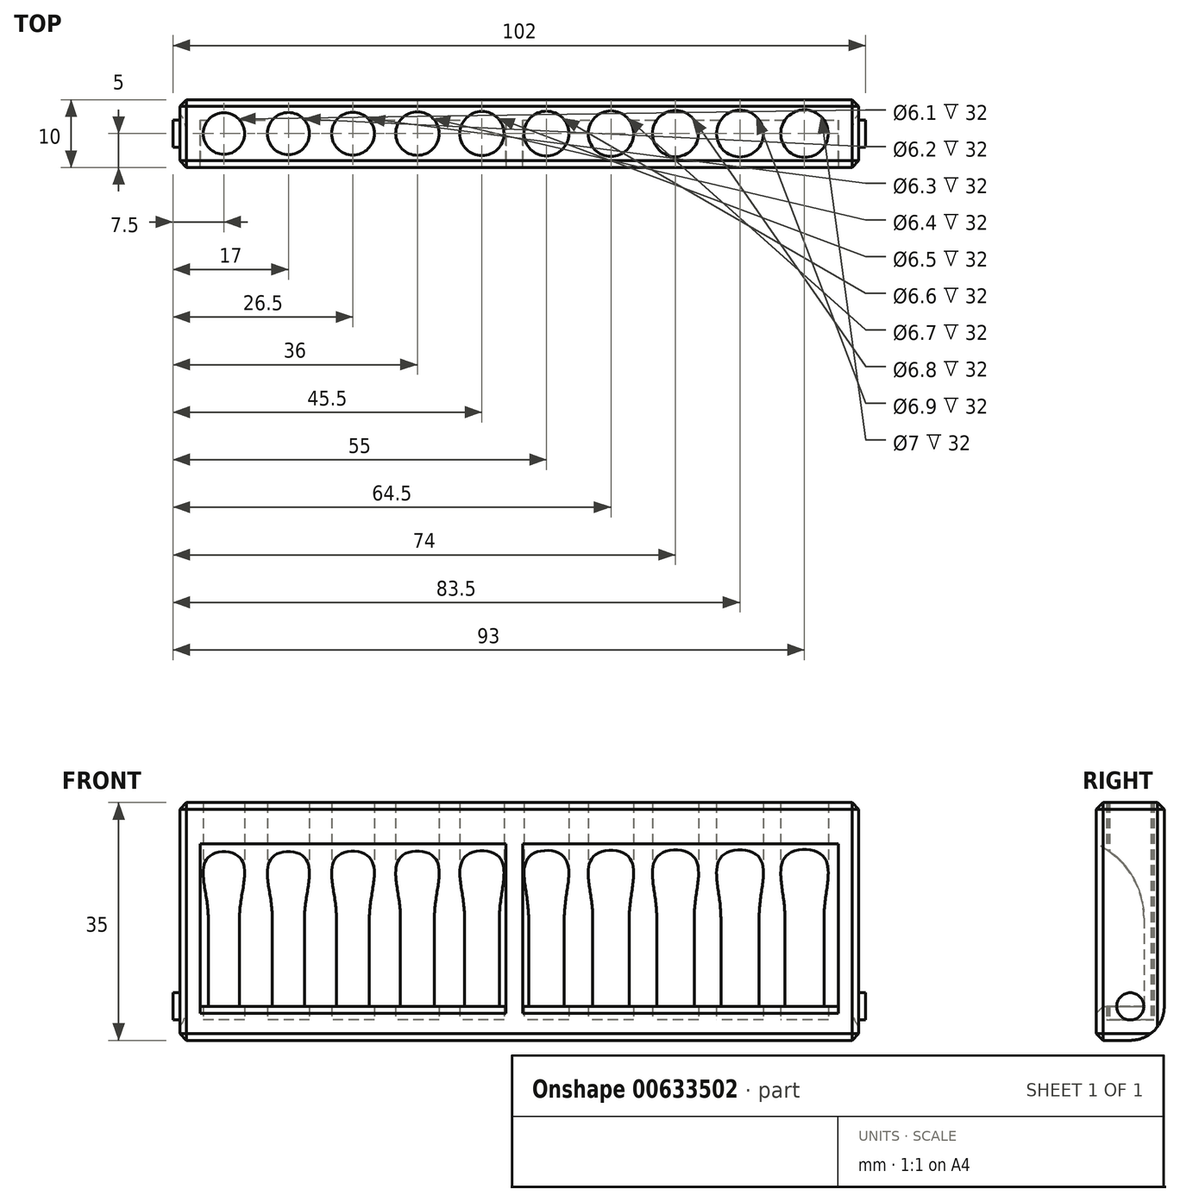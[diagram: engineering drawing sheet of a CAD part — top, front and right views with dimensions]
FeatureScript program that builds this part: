
annotation { "Feature Type Name" : "Feature", "Feature Type Description" : "" }
export const myFeature = defineFeature(function(context is Context, id is Id, definition is map)
    precondition{}
    {
        {
            var Q0;
            Q0=qCreatedBy(makeId("Top.planeOp"),FACE);
            var sketch = newSketch(context, id + "F0", { "sketchPlane" : qUnion([Q0])});
            skLineSegment(sketch, "E0.bottom", {"start": v(0, 0) * mm, "end": v(-100, 0) * mm});
            skLineSegment(sketch, "E0.top", {"start": v(0, -10) * mm, "end": v(-100, -10) * mm});
            skLineSegment(sketch, "E0.left", {"start": v(0, 0) * mm, "end": v(0, -10) * mm});
            skLineSegment(sketch, "E0.right", {"start": v(-100, 0) * mm, "end": v(-100, -10) * mm});
            skSolve(sketch);
        }
        {
            var Q0;
            Q0=qCreatedBy(makeId("Top.planeOp"),FACE);
            var sketch = newSketch(context, id + "F1", { "sketchPlane" : qUnion([Q0])});
            skLineSegment(sketch, "E1", {"start": v(0, 0) * mm, "end": v(0, -5) * mm, "construction": true});
            skLineSegment(sketch, "E2", {"start": v(0, -5) * mm, "end": v(-105.87, -5) * mm, "construction": true});
            skLineSegment(sketch, "E3", {"start": v(0, -5) * mm, "end": v(0, -25) * mm});
            skLineSegment(sketch, "E4", {"start": v(0, -25) * mm, "end": v(-8, -25) * mm});
            skLineSegment(sketch, "E5", {"start": v(-8, -25) * mm, "end": v(-8, 5) * mm, "construction": true});
            skCircle(sketch, "E6", {"center": v(-8, -5) * mm, "radius": 3.5 * mm});
            skCircle(sketch, "E7.1.0.0", {"center": v(-17.5, -5) * mm, "radius": 3.45 * mm});
            skCircle(sketch, "E7.2.0.0", {"center": v(-27, -5) * mm, "radius": 3.4 * mm});
            skCircle(sketch, "E7.3.0.0", {"center": v(-36.5, -5) * mm, "radius": 3.35 * mm});
            skCircle(sketch, "E7.4.0.0", {"center": v(-46, -5) * mm, "radius": 3.3 * mm});
            skCircle(sketch, "E7.5.0.0", {"center": v(-55.5, -5) * mm, "radius": 3.25 * mm});
            skCircle(sketch, "E7.6.0.0", {"center": v(-65, -5) * mm, "radius": 3.2 * mm});
            skCircle(sketch, "E7.7.0.0", {"center": v(-74.5, -5) * mm, "radius": 3.15 * mm});
            skCircle(sketch, "E7.8.0.0", {"center": v(-84, -5) * mm, "radius": 3.1 * mm});
            skCircle(sketch, "E7.9.0.0", {"center": v(-93.5, -5) * mm, "radius": 3.05 * mm});
            skLineSegment(sketch, "E7.direction1", {"start": v(-8, -5) * mm, "end": v(-17.5, -5) * mm, "construction": true});
            skSolve(sketch);
        }
        {
            var Q0;
            Q0=makeQuery(id+"F0.imprint","IMPRINT",FACE,{"disambiguationData":[TD([[makeQuery(id+"F0.imprint","IMPRINT",EDGE,{"derivedFrom":sQuery(id+"F0.wireOp",EDGE,"E0.bottom")}),1.0]])]});
            extrude(context, id + "F2", {"entities" : qUnion([Q0]), "depth" : 35 * mm, "offsetDistance" : 25 * mm});
        }
        {
            var Q0;
            Q0 = qSketchRegion(id + "F1", true);
            extrude(context, id + "F3", {"entities" : qUnion([Q0]), "operationType" : NewBodyOperationType.REMOVE, "depth" : 40 * mm, "offsetDistance" : 25 * mm, "hasSecondDirection" : true, "secondDirectionOppositeDirection" : false, "secondDirectionDepth" : 3 * mm});
        }
        {
            var Q0;
            Q0=qCreatedBy(makeId("Right.planeOp"),FACE);
            var sketch = newSketch(context, id + "F4", { "sketchPlane" : qUnion([Q0])});
            skLineSegment(sketch, "E8.bottom", {"start": v(-13, 5) * mm, "end": v(-3, 5) * mm});
            skLineSegment(sketch, "E8.top", {"start": v(-15, 30) * mm, "end": v(-13, 30) * mm});
            skLineSegment(sketch, "E8.left", {"start": v(-13, 5) * mm, "end": v(-13, 30) * mm});
            skLineSegment(sketch, "E8.right", {"start": v(-3, 5) * mm, "end": v(-3, 18) * mm});
            skPoint(sketch, "E9.visualSharp", {"position": v(-3, 30) * mm});
            skArc(sketch, "E9.filletArc", {"start": v(-3, 18) * mm, "mid": v(-6.51, 26.49) * mm, "end": v(-15, 30) * mm});
            skSolve(sketch);
        }
        {
            var Q0;
            Q0 = qSketchRegion(id + "F4", true);
            extrude(context, id + "F5", {"entities" : qUnion([Q0]), "operationType" : NewBodyOperationType.REMOVE, "oppositeDirection" : true, "depth" : 49.5 * mm, "offsetDistance" : 25 * mm, "hasSecondDirection" : true, "secondDirectionOppositeDirection" : true, "secondDirectionDepth" : 3 * mm});
        }
        {
            var Q0;
            Q0 = qSketchRegion(id + "F4", true);
            extrude(context, id + "F6", {"entities" : qUnion([Q0]), "operationType" : NewBodyOperationType.REMOVE, "oppositeDirection" : true, "depth" : 97 * mm, "offsetDistance" : 25 * mm, "hasSecondDirection" : true, "secondDirectionOppositeDirection" : true, "secondDirectionDepth" : 52 * mm});
        }
        {
            var Q0;
            Q0=makeQuery(id+"F2.opExtrude","CAP_EDGE",EDGE,{"disambiguationData":[OSD([sQuery(id+"F0.wireOp",EDGE,"E0.top")])],"isStart":false});
            var Q1;
            Q1=makeQuery(id+"F2.opExtrude","CAP_EDGE",EDGE,{"disambiguationData":[OSD([sQuery(id+"F0.wireOp",EDGE,"E0.right")])],"isStart":false});
            var Q2;
            Q2=makeQuery(id+"F2.opExtrude","CAP_EDGE",EDGE,{"disambiguationData":[OSD([sQuery(id+"F0.wireOp",EDGE,"E0.bottom")])],"isStart":false});
            var Q3;
            Q3=makeQuery(id+"F2.opExtrude","CAP_EDGE",EDGE,{"disambiguationData":[OSD([sQuery(id+"F0.wireOp",EDGE,"E0.left")])],"isStart":false});
            var Q4;
            Q4=makeQuery(id+"F2.opExtrude","SWEPT_EDGE",EDGE,{"disambiguationData":[OSD([sQuery(id+"F0.wireOp",EDGE,"E0.top"),sQuery(id+"F0.wireOp",EDGE,"E0.left")])]});
            var Q5;
            Q5=makeQuery(id+"F2.opExtrude","SWEPT_EDGE",EDGE,{"disambiguationData":[OSD([sQuery(id+"F0.wireOp",EDGE,"E0.bottom"),sQuery(id+"F0.wireOp",EDGE,"E0.left")])]});
            var Q6;
            Q6=makeQuery(id+"F2.opExtrude","CAP_EDGE",EDGE,{"disambiguationData":[OSD([sQuery(id+"F0.wireOp",EDGE,"E0.left")])],"isStart":true});
            var Q7;
            Q7=makeQuery(id+"F2.opExtrude","CAP_EDGE",EDGE,{"disambiguationData":[OSD([sQuery(id+"F0.wireOp",EDGE,"E0.top")])],"isStart":true});
            var Q8;
            Q8=makeQuery(id+"F2.opExtrude","SWEPT_EDGE",EDGE,{"disambiguationData":[OSD([sQuery(id+"F0.wireOp",EDGE,"E0.top"),sQuery(id+"F0.wireOp",EDGE,"E0.right")])]});
            var Q9;
            Q9=makeQuery(id+"F6.boolean.opBoolean","INTERSECT",EDGE,{"derivedFrom":[makeQuery(id+"F2.opExtrude","SWEPT_FACE",FACE,{"disambiguationData":[OSD([sQuery(id+"F0.wireOp",EDGE,"E0.top")])]}),makeQuery(id+"F6.opExtrude","SWEPT_FACE",FACE,{"disambiguationData":[OSD([sQuery(id+"F4.wireOp",EDGE,"E8.bottom")])]})]});
            var Q10;
            Q10=makeQuery(id+"F5.boolean.opBoolean","INTERSECT",EDGE,{"derivedFrom":[makeQuery(id+"F2.opExtrude","SWEPT_FACE",FACE,{"disambiguationData":[OSD([sQuery(id+"F0.wireOp",EDGE,"E0.top")])]}),makeQuery(id+"F5.opExtrude","SWEPT_FACE",FACE,{"disambiguationData":[OSD([sQuery(id+"F4.wireOp",EDGE,"E8.bottom")])]})]});
            var Q11;
            Q11=makeQuery(id+"F2.opExtrude","CAP_EDGE",EDGE,{"disambiguationData":[OSD([sQuery(id+"F0.wireOp",EDGE,"E0.right")])],"isStart":true});
            var Q12;
            Q12=makeQuery(id+"F2.opExtrude","SWEPT_FACE",FACE,{"disambiguationData":[OSD([sQuery(id+"F0.wireOp",EDGE,"E0.right")])]});
            chamfer(context, id + "F7", {"entities" : qUnion([Q0, Q1, Q2, Q3, Q4, Q5, Q6, Q7, Q8, Q9, Q10, Q11, Q12]), "width" : 1 * mm, "tangentPropagation" : true});
        }
        {
            var Q0;
            Q0=qCreatedBy(makeId("Right.planeOp"),FACE);
            var sketch = newSketch(context, id + "F8", { "sketchPlane" : qUnion([Q0])});
            skLineSegment(sketch, "E10", {"start": v(0, 0) * mm, "end": v(-5, 0) * mm, "construction": true});
            skLineSegment(sketch, "E11", {"start": v(-5, 0) * mm, "end": v(-5, 5) * mm, "construction": true});
            skCircle(sketch, "E12", {"center": v(-5, 5) * mm, "radius": 2 * mm});
            skSolve(sketch);
        }
        {
            var Q0;
            Q0=makeQuery(id+"F8.imprint","IMPRINT",FACE,{"disambiguationData":[TD([[makeQuery(id+"F8.imprint","IMPRINT",EDGE,{"derivedFrom":sQuery(id+"F8.wireOp",EDGE,"E12")}),1.0]])]});
            extrude(context, id + "F9", {"entities" : qUnion([Q0]), "operationType" : NewBodyOperationType.ADD, "oppositeDirection" : true, "depth" : 2 * mm, "offsetDistance" : 25 * mm, "hasSecondDirection" : true, "secondDirectionOppositeDirection" : false, "secondDirectionDepth" : 1 * mm});
        }
        {
            var Q0;
            Q0 = qSketchRegion(id + "F8", true);
            extrude(context, id + "F10", {"entities" : qUnion([Q0]), "operationType" : NewBodyOperationType.ADD, "oppositeDirection" : true, "depth" : 101 * mm, "offsetDistance" : 25 * mm, "hasSecondDirection" : true, "secondDirectionOppositeDirection" : true, "secondDirectionDepth" : 99 * mm});
        }
        {
            var Q0;
            Q0=makeQuery(id+"F2.opExtrude","CAP_EDGE",EDGE,{"disambiguationData":[OSD([sQuery(id+"F0.wireOp",EDGE,"E0.bottom")])],"isStart":true});
            fillet(context, id + "F11", {"entities" : qUnion([Q0]), "radius" : 5 * mm, "tangentPropagation" : true, "allowEdgeOverflow" : false});
        }
    });
